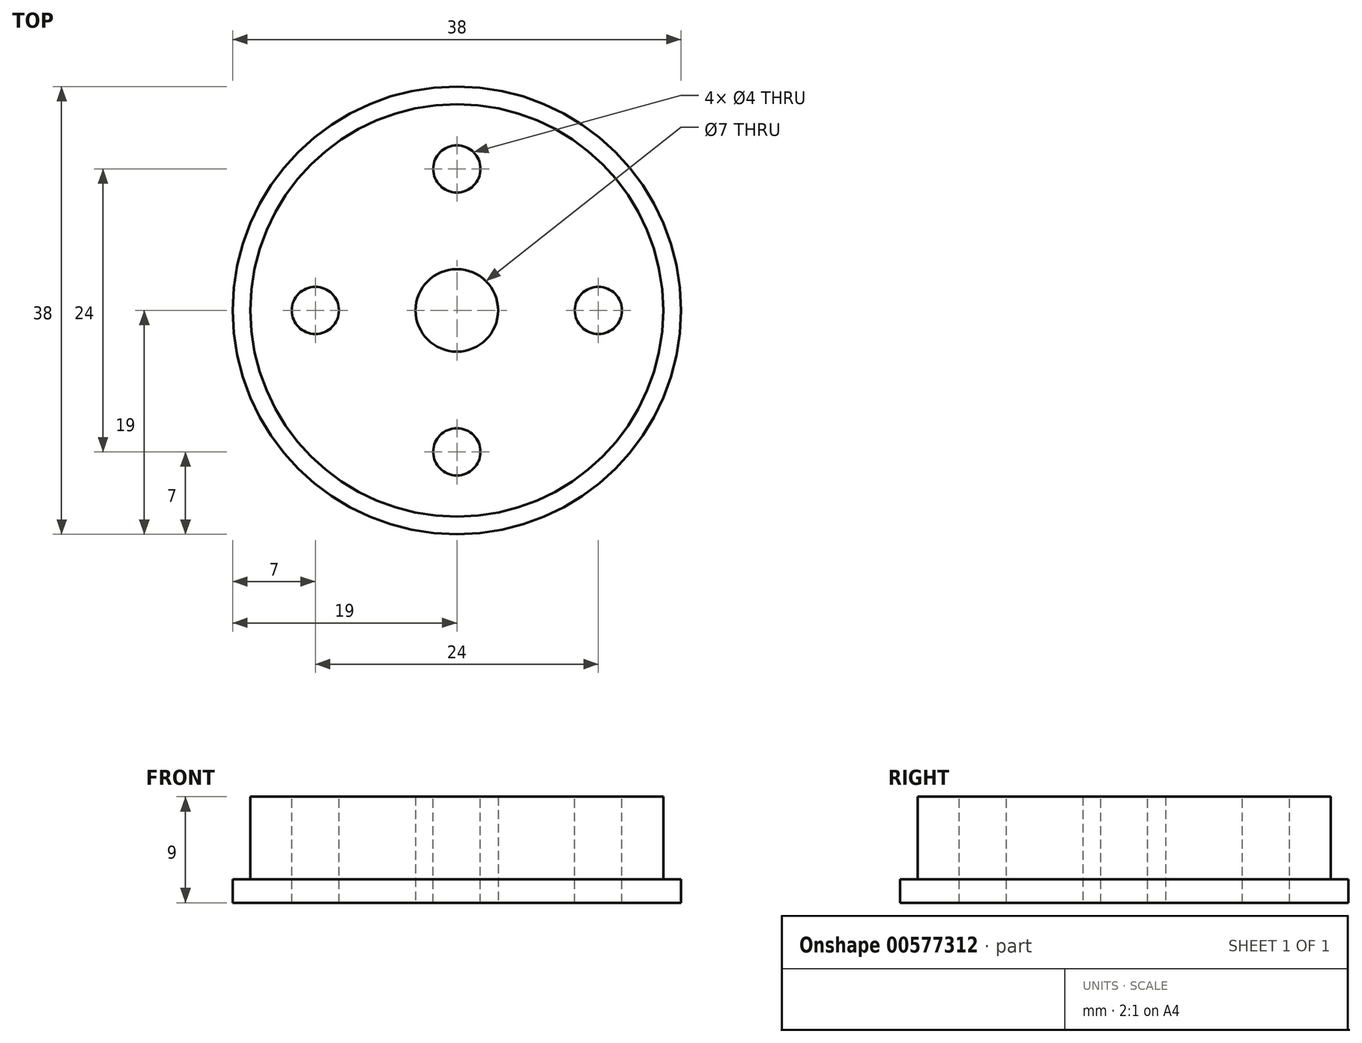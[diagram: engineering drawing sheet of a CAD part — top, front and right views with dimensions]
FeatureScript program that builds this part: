
annotation { "Feature Type Name" : "Feature", "Feature Type Description" : "" }
export const myFeature = defineFeature(function(context is Context, id is Id, definition is map)
    precondition{}
    {
        {
            var Q0;
            Q0=qCreatedBy(makeId("Top.planeOp"),FACE);
            var sketch = newSketch(context, id + "F0", { "sketchPlane" : qUnion([Q0])});
            skCircle(sketch, "E0", {"center": v(0, 0) * mm, "radius": 3.5 * mm});
            skCircle(sketch, "E1", {"center": v(0, 0) * mm, "radius": 19 * mm});
            skSolve(sketch);
        }
        {
            var Q0;
            Q0 = qSketchRegion(id + "F0", true);
            extrude(context, id + "F1", {"entities" : qUnion([Q0]), "depth" : 2 * mm, "offsetDistance" : 25 * mm});
        }
        {
            var Q0;
            Q0=makeQuery(id+"F1.opExtrude","CAP_FACE",FACE,{"disambiguationData":[OSD([sQuery(id+"F0.wireOp",EDGE,"E0"),sQuery(id+"F0.wireOp",EDGE,"E1")])],"isStart":false});
            var sketch = newSketch(context, id + "F2", { "sketchPlane" : qUnion([Q0])});
            skCircle(sketch, "E2", {"center": v(0, 0) * mm, "radius": 17.5 * mm});
            skCircle(sketch, "E3", {"center": v(0, 0) * mm, "radius": 3.5 * mm});
            skSolve(sketch);
        }
        {
            var Q0;
            Q0 = qSketchRegion(id + "F2", true);
            extrude(context, id + "F3", {"entities" : qUnion([Q0]), "operationType" : NewBodyOperationType.ADD, "depth" : 7 * mm, "offsetDistance" : 25 * mm});
        }
        {
            var Q0;
            Q0=makeQuery(id+"F3.opExtrude","CAP_FACE",FACE,{"disambiguationData":[OSD([sQuery(id+"F2.wireOp",EDGE,"E2"),sQuery(id+"F2.wireOp",EDGE,"E3")])],"isStart":false});
            var sketch = newSketch(context, id + "F4", { "sketchPlane" : qUnion([Q0])});
            skCircle(sketch, "E4", {"center": v(0, 12) * mm, "radius": 2 * mm});
            skCircle(sketch, "E5.1.0", {"center": v(-12, 0) * mm, "radius": 2 * mm});
            skCircle(sketch, "E5.2.0", {"center": v(0, -12) * mm, "radius": 2 * mm});
            skPoint(sketch, "E5.center", {"position": v(0, 0) * mm});
            skCircle(sketch, "E6.1.3.0", {"center": v(12, 0) * mm, "radius": 2 * mm});
            skSolve(sketch);
        }
        {
            var Q0;
            Q0 = qSketchRegion(id + "F4", true);
            extrude(context, id + "F5", {"entities" : qUnion([Q0]), "operationType" : NewBodyOperationType.REMOVE, "oppositeDirection" : true, "depth" : 25 * mm, "offsetDistance" : 25 * mm});
        }
    });
